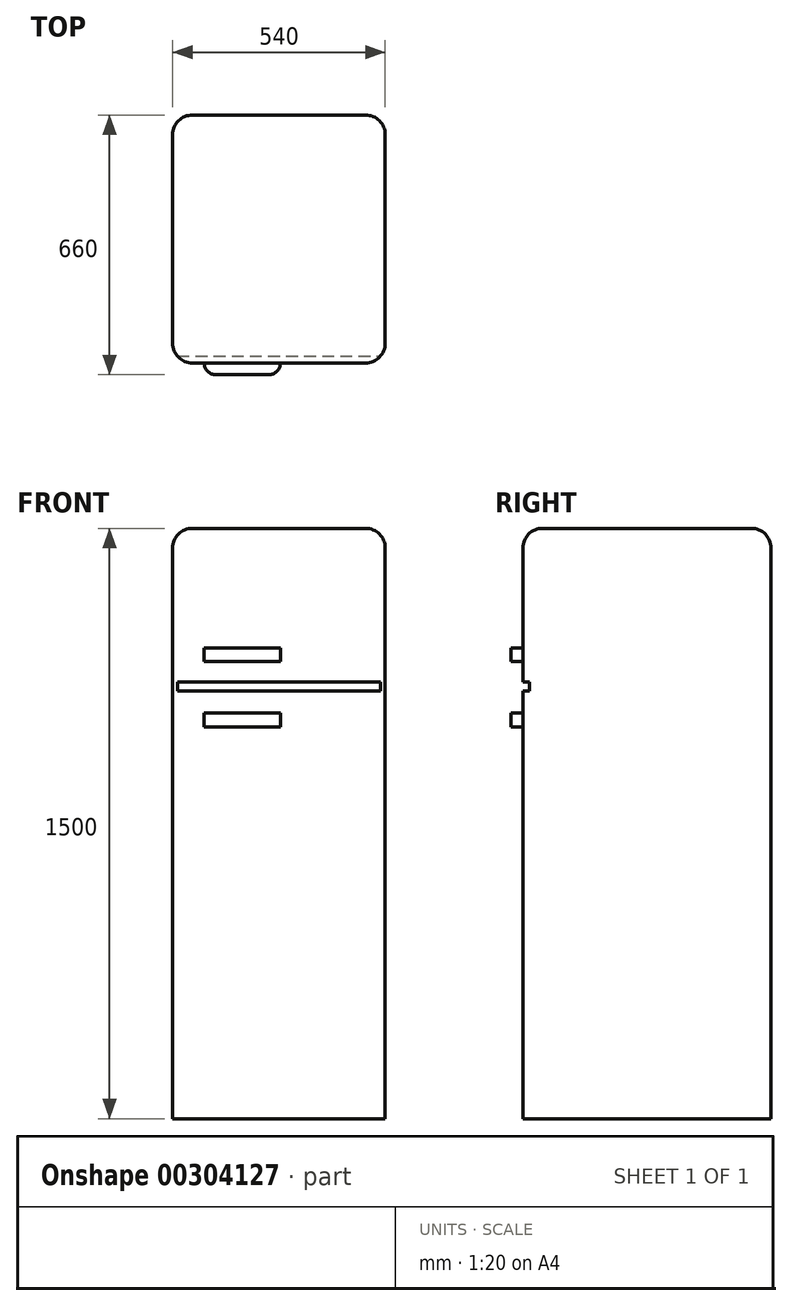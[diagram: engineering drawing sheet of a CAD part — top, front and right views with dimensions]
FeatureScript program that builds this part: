
annotation { "Feature Type Name" : "Feature", "Feature Type Description" : "" }
export const myFeature = defineFeature(function(context is Context, id is Id, definition is map)
    precondition{}
    {
        {
            var Q0;
            Q0=qCreatedBy(makeId("Top.planeOp"),FACE);
            var sketch = newSketch(context, id + "F0", { "sketchPlane" : qUnion([Q0])});
            skLineSegment(sketch, "E0.bottom", {"start": v(-283.39, 316.4) * mm, "end": v(256.61, 316.4) * mm});
            skLineSegment(sketch, "E0.top", {"start": v(-283.39, -313.6) * mm, "end": v(256.61, -313.6) * mm});
            skLineSegment(sketch, "E0.left", {"start": v(-283.39, 316.4) * mm, "end": v(-283.39, -313.6) * mm});
            skLineSegment(sketch, "E0.right", {"start": v(256.61, 316.4) * mm, "end": v(256.61, -313.6) * mm});
            skSolve(sketch);
        }
        {
            var Q0;
            Q0=makeQuery(id+"F0.imprint","IMPRINT",FACE,{"disambiguationData":[TD([[makeQuery(id+"F0.imprint","IMPRINT",EDGE,{"derivedFrom":sQuery(id+"F0.wireOp",EDGE,"E0.bottom")}),-1.0]])]});
            extrude(context, id + "F1", {"entities" : qUnion([Q0]), "depth" : 1500 * mm, "offsetDistance" : 25 * mm});
        }
        {
            var Q0;
            Q0=makeQuery(id+"F1.opExtrude","CAP_EDGE",EDGE,{"disambiguationData":[OSD([sQuery(id+"F0.wireOp",EDGE,"E0.top")])],"isStart":false});
            var Q1;
            Q1=makeQuery(id+"F1.opExtrude","CAP_EDGE",EDGE,{"disambiguationData":[OSD([sQuery(id+"F0.wireOp",EDGE,"E0.left")])],"isStart":false});
            var Q2;
            Q2=makeQuery(id+"F1.opExtrude","SWEPT_EDGE",EDGE,{"disambiguationData":[OSD([sQuery(id+"F0.wireOp",EDGE,"E0.top"),sQuery(id+"F0.wireOp",EDGE,"E0.left")])]});
            var Q3;
            Q3=makeQuery(id+"F1.opExtrude","SWEPT_EDGE",EDGE,{"disambiguationData":[OSD([sQuery(id+"F0.wireOp",EDGE,"E0.top"),sQuery(id+"F0.wireOp",EDGE,"E0.right")])]});
            var Q4;
            Q4=makeQuery(id+"F1.opExtrude","CAP_EDGE",EDGE,{"disambiguationData":[OSD([sQuery(id+"F0.wireOp",EDGE,"E0.right")])],"isStart":false});
            var Q5;
            Q5=makeQuery(id+"F1.opExtrude","SWEPT_EDGE",EDGE,{"disambiguationData":[OSD([sQuery(id+"F0.wireOp",EDGE,"E0.bottom"),sQuery(id+"F0.wireOp",EDGE,"E0.right")])]});
            var Q6;
            Q6=makeQuery(id+"F1.opExtrude","CAP_EDGE",EDGE,{"disambiguationData":[OSD([sQuery(id+"F0.wireOp",EDGE,"E0.bottom")])],"isStart":false});
            var Q7;
            Q7=makeQuery(id+"F1.opExtrude","SWEPT_EDGE",EDGE,{"disambiguationData":[OSD([sQuery(id+"F0.wireOp",EDGE,"E0.bottom"),sQuery(id+"F0.wireOp",EDGE,"E0.left")])]});
            fillet(context, id + "F2", {"entities" : qUnion([Q0, Q1, Q2, Q3, Q4, Q5, Q6, Q7]), "radius" : 50 * mm, "tangentPropagation" : true, "allowEdgeOverflow" : false});
        }
        {
            var Q0;
            Q0=makeQuery(id+"F1.opExtrude","SWEPT_FACE",FACE,{"disambiguationData":[OSD([sQuery(id+"F0.wireOp",EDGE,"E0.right")])]});
            var sketch = newSketch(context, id + "F3", { "sketchPlane" : qUnion([Q0])});
            skLineSegment(sketch, "E1.bottom", {"start": v(-338.59, 1109.15) * mm, "end": v(-296.46, 1109.15) * mm});
            skLineSegment(sketch, "E1.top", {"start": v(-338.59, 1086.06) * mm, "end": v(-296.46, 1086.06) * mm});
            skLineSegment(sketch, "E1.left", {"start": v(-338.59, 1109.15) * mm, "end": v(-338.59, 1086.06) * mm});
            skLineSegment(sketch, "E1.right", {"start": v(-296.46, 1109.15) * mm, "end": v(-296.46, 1086.06) * mm});
            skSolve(sketch);
        }
        {
            var Q0;
            Q0=makeQuery(id+"F3.imprint","IMPRINT",FACE,{"disambiguationData":[TD([[makeQuery(id+"F3.imprint","IMPRINT",EDGE,{"derivedFrom":sQuery(id+"F3.wireOp",EDGE,"E1.bottom")}),-1.0]])]});
            extrude(context, id + "F4", {"entities" : qUnion([Q0]), "operationType" : NewBodyOperationType.REMOVE, "oppositeDirection" : true, "depth" : 1000 * mm, "offsetDistance" : 25 * mm});
        }
        {
            var Q0;
            {var subQ1=sQuery(id+"F0.wireOp",EDGE,"E0.top");Q0=makeQuery(id+"F4.boolean.opBoolean","SPLIT",FACE,{"disambiguationData":[TD([makeQuery(id+"F2.opFillet","BLEND_FACE",FACE,{"disambiguationData":[OSD([subQ1])]})])],"derivedFrom":makeQuery(id+"F1.opExtrude","SWEPT_FACE",FACE,{"disambiguationData":[OSD([subQ1])]})});}
            var sketch = newSketch(context, id + "F5", { "sketchPlane" : qUnion([Q0])});
            skLineSegment(sketch, "E2.bottom", {"start": v(-203.08, 1196.35) * mm, "end": v(-9.81, 1196.35) * mm});
            skLineSegment(sketch, "E2.top", {"start": v(-203.08, 1161.06) * mm, "end": v(-9.81, 1161.06) * mm});
            skLineSegment(sketch, "E2.left", {"start": v(-203.08, 1196.35) * mm, "end": v(-203.08, 1161.06) * mm});
            skLineSegment(sketch, "E2.right", {"start": v(-9.81, 1196.35) * mm, "end": v(-9.81, 1161.06) * mm});
            skLineSegment(sketch, "E3.bottom", {"start": v(-203.08, 1031.06) * mm, "end": v(-9.81, 1031.06) * mm});
            skLineSegment(sketch, "E3.top", {"start": v(-203.08, 995.78) * mm, "end": v(-9.81, 995.78) * mm});
            skLineSegment(sketch, "E3.left", {"start": v(-203.08, 1031.06) * mm, "end": v(-203.08, 995.78) * mm});
            skLineSegment(sketch, "E3.right", {"start": v(-9.81, 1031.06) * mm, "end": v(-9.81, 995.78) * mm});
            skSolve(sketch);
        }
        {
            var Q0;
            Q0=makeQuery(id+"F5.imprint","IMPRINT",FACE,{"disambiguationData":[TD([[makeQuery(id+"F5.imprint","IMPRINT",EDGE,{"derivedFrom":sQuery(id+"F5.wireOp",EDGE,"E2.bottom")}),-1.0]])]});
            var Q1;
            Q1=makeQuery(id+"F5.imprint","IMPRINT",FACE,{"disambiguationData":[TD([[makeQuery(id+"F5.imprint","IMPRINT",EDGE,{"derivedFrom":sQuery(id+"F5.wireOp",EDGE,"E3.bottom")}),-1.0]])]});
            extrude(context, id + "F6", {"entities" : qUnion([Q0, Q1]), "depth" : 30 * mm, "offsetDistance" : 25 * mm});
        }
        {
            var Q0;
            Q0=makeQuery(id+"F6.opExtrude","CAP_EDGE",EDGE,{"disambiguationData":[OSD([sQuery(id+"F5.wireOp",EDGE,"E2.left")])],"isStart":false});
            var Q1;
            Q1=makeQuery(id+"F6.opExtrude","CAP_EDGE",EDGE,{"disambiguationData":[OSD([sQuery(id+"F5.wireOp",EDGE,"E2.right")])],"isStart":false});
            var Q2;
            Q2=makeQuery(id+"F6.opExtrude","CAP_EDGE",EDGE,{"disambiguationData":[OSD([sQuery(id+"F5.wireOp",EDGE,"E3.left")])],"isStart":false});
            var Q3;
            Q3=makeQuery(id+"F6.opExtrude","CAP_EDGE",EDGE,{"disambiguationData":[OSD([sQuery(id+"F5.wireOp",EDGE,"E3.right")])],"isStart":false});
            fillet(context, id + "F7", {"entities" : qUnion([Q0, Q1, Q2, Q3]), "radius" : 30 * mm, "tangentPropagation" : true, "allowEdgeOverflow" : false});
        }
    });
